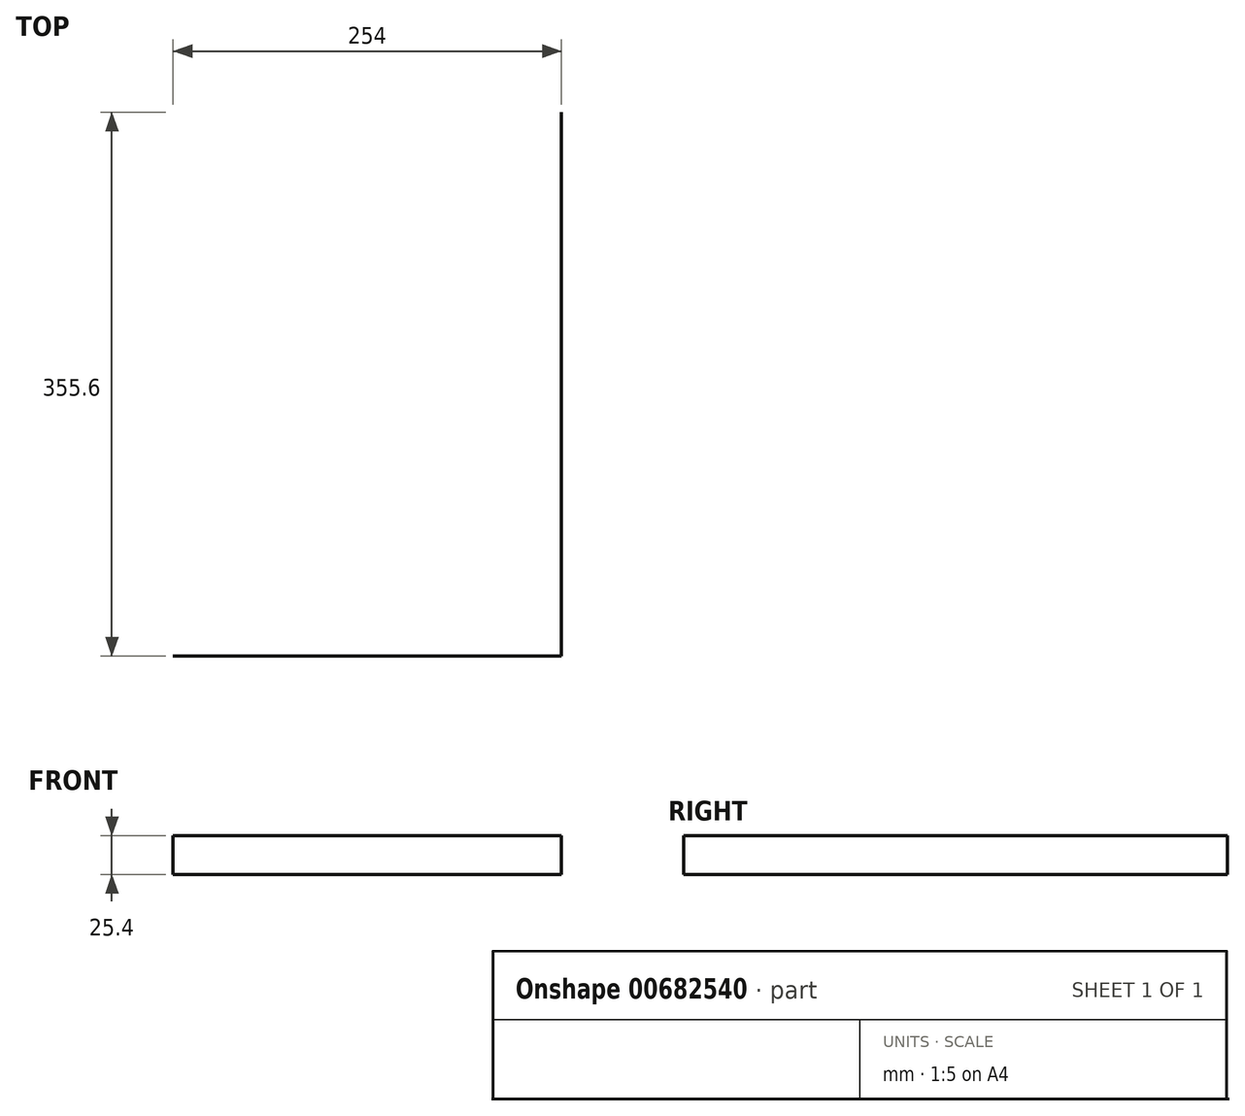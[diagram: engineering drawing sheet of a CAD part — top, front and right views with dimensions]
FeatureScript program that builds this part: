
annotation { "Feature Type Name" : "Feature", "Feature Type Description" : "" }
export const myFeature = defineFeature(function(context is Context, id is Id, definition is map)
    precondition{}
    {
        {
            var Q0;
            Q0=qCreatedBy(makeId("Top.planeOp"),FACE);
            var sketch = newSketch(context, id + "F0", { "sketchPlane" : qUnion([Q0])});
            skLineSegment(sketch, "E0.bottom", {"start": v(0, 0) * mm, "end": v(254, 0) * mm});
            skLineSegment(sketch, "E0.top", {"start": v(0, 355.6) * mm, "end": v(254, 355.6) * mm});
            skLineSegment(sketch, "E0.left", {"start": v(0, 0) * mm, "end": v(0, 355.6) * mm});
            skLineSegment(sketch, "E0.right", {"start": v(254, 0) * mm, "end": v(254, 355.6) * mm});
            skSolve(sketch);
        }
        {
            var Q0;
            Q0=sQuery(id+"F0.wireOp",EDGE,"E0.right");
            var Q1;
            Q1=sQuery(id+"F0.wireOp",EDGE,"E0.bottom");
            extrude(context, id + "F1", {"bodyType" : ToolBodyType.SURFACE, "surfaceEntities" : qUnion([Q0, Q1]), "depth" : 25.4 * mm, "offsetDistance" : 25.4 * mm});
        }
    });
